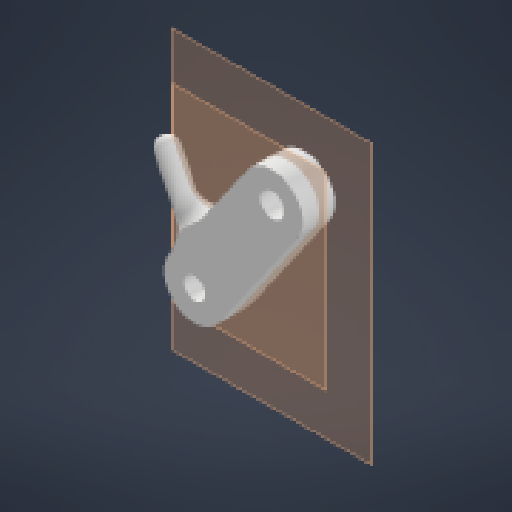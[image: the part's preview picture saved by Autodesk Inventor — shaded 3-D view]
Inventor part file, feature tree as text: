
AUTODESK INVENTOR PART (.ipt)
format: ipt  version: 2024.1 (Build 281209000, 209)  size: 213,504 bytes
history: native  units: in
note: dims shown in document units (in); Inventor stores cm internally (conversion verified against a paired STEP export)
features: other x3, plane x2, extrude x2, fillet x2, sketch x2, reference x1, projected_geometry x1
ambient origin geometry x8: Origin, YZ Plane, XZ Plane, XY Plane, X Axis, Y Axis, Z Axis, Center Point
bodies: Solid1 (feature_tree)
feature tree (13):
  plane  "Work Plane1"
  extrude  "Extrusion1"  Depth=0.45in
  plane  "Work Plane2"
  extrude  "Extrusion2"  TaperAngle=60.0deg  [1 undecoded]
  fillet  "Fillet1"  Radius=0.24in
  fillet  "Fillet2"  Radius=0.75in
  sketch  "Sketch1"  dims[d0=0.45in d1=0.45in]
  reference  "Reference1"
  sketch  "Sketch2"  dims[d2=0.75in d3=60.0deg d4=0.24in d5=0.0in d6=0.75in d7=60.0deg d8=0.075in d9=0.075in d10=0.15in d11=0.0in d12=0.075in d13=0.145in]
  projected_geometry  "Projected Loop1"
  other  "<userpath>\Documents\School\FallCAD\Trebuchet\Trebuchet.iam"
  other  "Trebuchet.iam"
  other  "CarabinerThrowMount:1"
note: 1 required parameter value undecoded (feature->parameter linkage not recoverable at this tier; creation-order binding heuristic only, values carry confidence <= 0.55)
